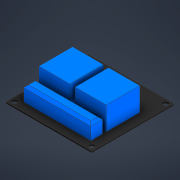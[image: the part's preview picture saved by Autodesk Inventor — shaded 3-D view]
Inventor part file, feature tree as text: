
AUTODESK INVENTOR PART (.ipt)
format: ipt  version: 2021 (Build 250183000, 183)  size: 143,360 bytes
history: native  units: mm
features: extrude x3, other x1, sketch x1, chamfer x1
ambient origin geometry x8: Origin, YZ Plane, XZ Plane, XY Plane, X Axis, Y Axis, Z Axis, Center Point
bodies: Volumenkörper1 (feature_tree)
feature tree (6):
  other  "Relais"
  sketch  "Skizze1"  dims[d0=51.0mm d1=49.0mm d2=3.0mm d3=2.5mm d4=2.5mm d5=7.0mm d6=5.0mm d7=40.0mm d8=18.5mm d9=20.0mm d10=1.0mm d11=0.0mm d12=10.0mm d13=0.0mm d14=15.0mm d15=0.0mm d16=1.5mm d17=2.0mm d18=45.0deg]
  extrude  "Extrusion1"  Depth=49.0mm
  extrude  "Extrusion2"  Depth=3.0mm
  extrude  "Extrusion3"  Depth=1.5mm
  chamfer  "Fase1"  Distance=2.5mm
